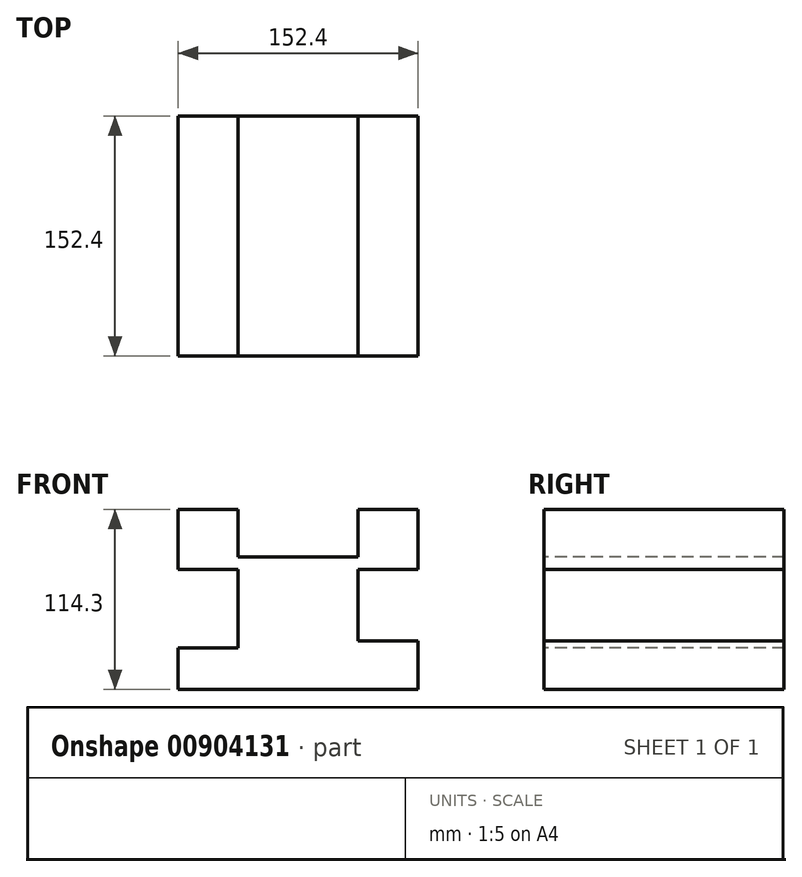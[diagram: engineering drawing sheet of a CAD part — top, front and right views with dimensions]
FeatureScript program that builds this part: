
annotation { "Feature Type Name" : "Feature", "Feature Type Description" : "" }
export const myFeature = defineFeature(function(context is Context, id is Id, definition is map)
    precondition{}
    {
        {
            var Q0;
            Q0=qCreatedBy(makeId("Front.planeOp"),FACE);
            var sketch = newSketch(context, id + "F0", { "sketchPlane" : qUnion([Q0])});
            skLineSegment(sketch, "E0.bottom", {"start": v(-76.2, 57.15) * mm, "end": v(76.2, 57.15) * mm});
            skLineSegment(sketch, "E0.top", {"start": v(-76.2, -57.15) * mm, "end": v(76.2, -57.15) * mm});
            skLineSegment(sketch, "E0.left", {"start": v(-76.2, 57.15) * mm, "end": v(-76.2, -57.15) * mm});
            skLineSegment(sketch, "E0.right", {"start": v(76.2, 57.15) * mm, "end": v(76.2, -57.15) * mm});
            skPoint(sketch, "E0.middle", {"position": v(0, 0) * mm});
            skSolve(sketch);
        }
        {
            var Q0;
            Q0=makeQuery(id+"F0.imprint","IMPRINT",FACE,{"disambiguationData":[TD([[makeQuery(id+"F0.imprint","IMPRINT",EDGE,{"derivedFrom":sQuery(id+"F0.wireOp",EDGE,"E0.bottom")}),-1.0]])]});
            extrude(context, id + "F1", {"entities" : qUnion([Q0]), "depth" : 152.4 * mm, "offsetDistance" : 25.4 * mm});
        }
        {
            var Q0;
            Q0=makeQuery(id+"F1.opExtrude","CAP_FACE",FACE,{"disambiguationData":[OSD([sQuery(id+"F0.wireOp",EDGE,"E0.bottom"),sQuery(id+"F0.wireOp",EDGE,"E0.top"),sQuery(id+"F0.wireOp",EDGE,"E0.left"),sQuery(id+"F0.wireOp",EDGE,"E0.right")])],"isStart":false});
            var sketch = newSketch(context, id + "F2", { "sketchPlane" : qUnion([Q0])});
            skLineSegment(sketch, "E1", {"start": v(-76.2, -57.15) * mm, "end": v(-76.2, -30.68) * mm});
            skLineSegment(sketch, "E2", {"start": v(-76.2, -30.68) * mm, "end": v(-38.1, -30.68) * mm});
            skLineSegment(sketch, "E3", {"start": v(-76.2, 57.15) * mm, "end": v(-76.2, 19.05) * mm});
            skLineSegment(sketch, "E4", {"start": v(-38.1, -30.68) * mm, "end": v(-38.1, 19.05) * mm});
            skLineSegment(sketch, "E5", {"start": v(-76.2, 19.05) * mm, "end": v(-38.1, 19.05) * mm});
            skLineSegment(sketch, "E6", {"start": v(76.2, 57.15) * mm, "end": v(76.2, 19.05) * mm});
            skLineSegment(sketch, "E7", {"start": v(76.2, 19.05) * mm, "end": v(38.1, 19.05) * mm});
            skLineSegment(sketch, "E8", {"start": v(38.1, 19.05) * mm, "end": v(38.1, -26.36) * mm});
            skLineSegment(sketch, "E9", {"start": v(38.1, -26.36) * mm, "end": v(76.2, -26.36) * mm});
            skLineSegment(sketch, "E10", {"start": v(-38.1, 57.15) * mm, "end": v(-38.1, 26.9) * mm});
            skLineSegment(sketch, "E11", {"start": v(-38.1, 26.9) * mm, "end": v(38.1, 26.9) * mm});
            skLineSegment(sketch, "E12", {"start": v(38.1, 26.9) * mm, "end": v(38.1, 57.15) * mm});
            skSolve(sketch);
        }
        {
            var Q0;
            {var subQ0=sQuery(id+"F2.wireOp",EDGE,"E10");Q0=makeQuery(id+"F2.imprint","IMPRINT",FACE,{"disambiguationData":[TD([[makeQuery(id+"F2.imprint","IMPRINT",EDGE,{"derivedFrom":subQ0}),1.0]])]});}
            extrude(context, id + "F3", {"entities" : qUnion([Q0]), "operationType" : NewBodyOperationType.REMOVE, "endBound" : BoundingType.THROUGH_ALL, "oppositeDirection" : true, "depth" : 25.4 * mm, "offsetDistance" : 25.4 * mm});
        }
        {
            var Q0;
            {var subQ0=sQuery(id+"F2.wireOp",EDGE,"E2");Q0=makeQuery(id+"F2.imprint","IMPRINT",FACE,{"disambiguationData":[TD([[makeQuery(id+"F2.imprint","IMPRINT",EDGE,{"derivedFrom":subQ0}),1.0]])]});}
            extrude(context, id + "F4", {"entities" : qUnion([Q0]), "operationType" : NewBodyOperationType.REMOVE, "endBound" : BoundingType.THROUGH_ALL, "oppositeDirection" : true, "depth" : 25.4 * mm, "offsetDistance" : 25.4 * mm});
        }
        {
            var Q0;
            {var subQ0=sQuery(id+"F2.wireOp",EDGE,"E7");Q0=makeQuery(id+"F2.imprint","IMPRINT",FACE,{"disambiguationData":[TD([[makeQuery(id+"F2.imprint","IMPRINT",EDGE,{"derivedFrom":subQ0}),1.0]])]});}
            extrude(context, id + "F5", {"entities" : qUnion([Q0]), "operationType" : NewBodyOperationType.REMOVE, "endBound" : BoundingType.THROUGH_ALL, "oppositeDirection" : true, "depth" : 25.4 * mm, "offsetDistance" : 25.4 * mm});
        }
    });
